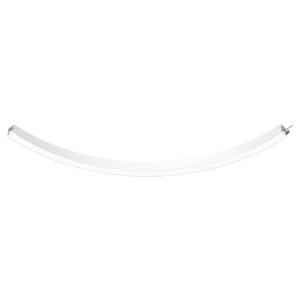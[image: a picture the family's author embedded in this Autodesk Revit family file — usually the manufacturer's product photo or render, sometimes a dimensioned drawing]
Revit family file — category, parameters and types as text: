
# Revit family: super-g_slim_super_g_slim_dir_ind_3000_90deg_hl_ps_led_72w__11520lm__3000k__cri80_430-3830_ded4
name_source: partatom
category: Leuchten
revit_build: Autodesk Revit 2016 (Build: 20190508_0715(x64)
units: mm (PartAtom-declared; Revit-internal decimal feet)

## family parameters
Basisbauteil = Fläche
Beim Laden mit Abzugskörper schneiden = Nein
Bemaßung runder Anschluss = Durchmesser verwenden
Gemeinsam genutzt = Nein
Lichtquelle = Nein
Raumberechnungspunkt = Nein
Teiletyp = Normal

## types (1)
- 430-3830-D01 (1 x LED, 720 lm, 3000K)
    Beschreibung = The insert consists of aluminum-extruded profile. Charming SOFT-EDGE design ensure unparalleled styling. The ballast is integrated and allows for an operation with 220-240V (50/60Hz). SUPER-G SLIM (# 430-3830) ist not dimmable (on/off).
    CIE Flux Codes = 48 79 96 66 85
    Color Rendering = 1B/80…89
    Color Temperature = 3000K
    Height = 90 mm
    Hersteller = Prolicht
    Lamp Light Flux = 720 lm
    Lamp count = 1
    Lampe = 1 x LED
    Length = 147 mm
    Luminous efficacy = 122 lm/W
    ModVariant = Nein
    Modell = 430-3830
    Mounting Place = Ceiling
    Mounting Type = Pendant
    Number of Poles = 1
    OnlyDefault = Ja
    Power Factor = 1
    Product Name = SUPER-G SLIM__SUPER G SLIM DIR/IND 3000/90° HL PS LED 72W  11520lm  3000K  CRI80
    Product group = Suspended profile systems
    ProductGroupID = 944
    Protection Class = Protection class
    Protection Degree = Degree of protection
    RLX_Detail_Level = 1
    RlxData = <blob elided: 32141 chars, md5=ab21587b>
    Scheinlast = 80 VA
    Socket = socket
    Standby Power = 0 W
    System Light Flux = 9746 lm
    System Power = 80 W
    Typenbild = 430-3830.jpg
    URL = http://relux.com
    VarID = 430-3830-d01
    Voltage = 0 V
    Vorgabe-Ansicht = 1800 mm
    Weight = 0.00 kg
    Width = 65 mm

## geometry (parser evidence)
native form markers: Sweep x64
no freeform markers — native parametric forms only
